# Revit family: Soft Lounge
name_source: partatom
category: Furniture
units: mm (PartAtom-declared; Revit-internal decimal feet)

## family parameters
Always vertical = Yes
Cut with Voids When Loaded = No
OmniClass Number = 23.40.20.00
OmniClass Title = General Furniture and Specialties
Room Calculation Point = No
Shared = No
Work Plane-Based = No

## types (6) — shared parameters
Default Elevation = 0' - 0"
Manufacturer = AIS Inc
Product = SOFT LOUNGE
URL = https://www.ais-inc.com

## per-type parameters (varying)
| type | Description | LSOFT1 | LSOFT1C | LSOFT2 | LSOFT2C | LSOFT3 | LSOFT3C |
| LSOFT1 | 40"Wx33"Dx29"H Soft Lounge Club Chair | Yes | No | No | No | No | No |
| LSOFT1C | 40"Wx33"Dx29"H Soft Lounge Club Chair, Configurable | No | Yes | No | No | No | No |
| LSOFT2 | 66"Wx33"Dx29"H Soft Lounge 2-Seater | No | No | Yes | No | No | No |
| LSOFT2C | 66"Wx33"Dx29"H Soft Lounge 2-Seater, Configurable | No | No | No | Yes | No | No |
| LSOFT3 | 87.5"Wx33"Dx29"H Soft Lounge 3-Seater | No | No | No | No | Yes | No |
| LSOFT3C | 87.5"Wx33"Dx29"H Soft Lounge 3-Seater, Configurable | No | No | No | No | No | Yes |

note: column(s) folded — value = type name in every type: Model

## geometry (parser evidence)
native form markers: Sweep x3
no freeform markers — native parametric forms only
